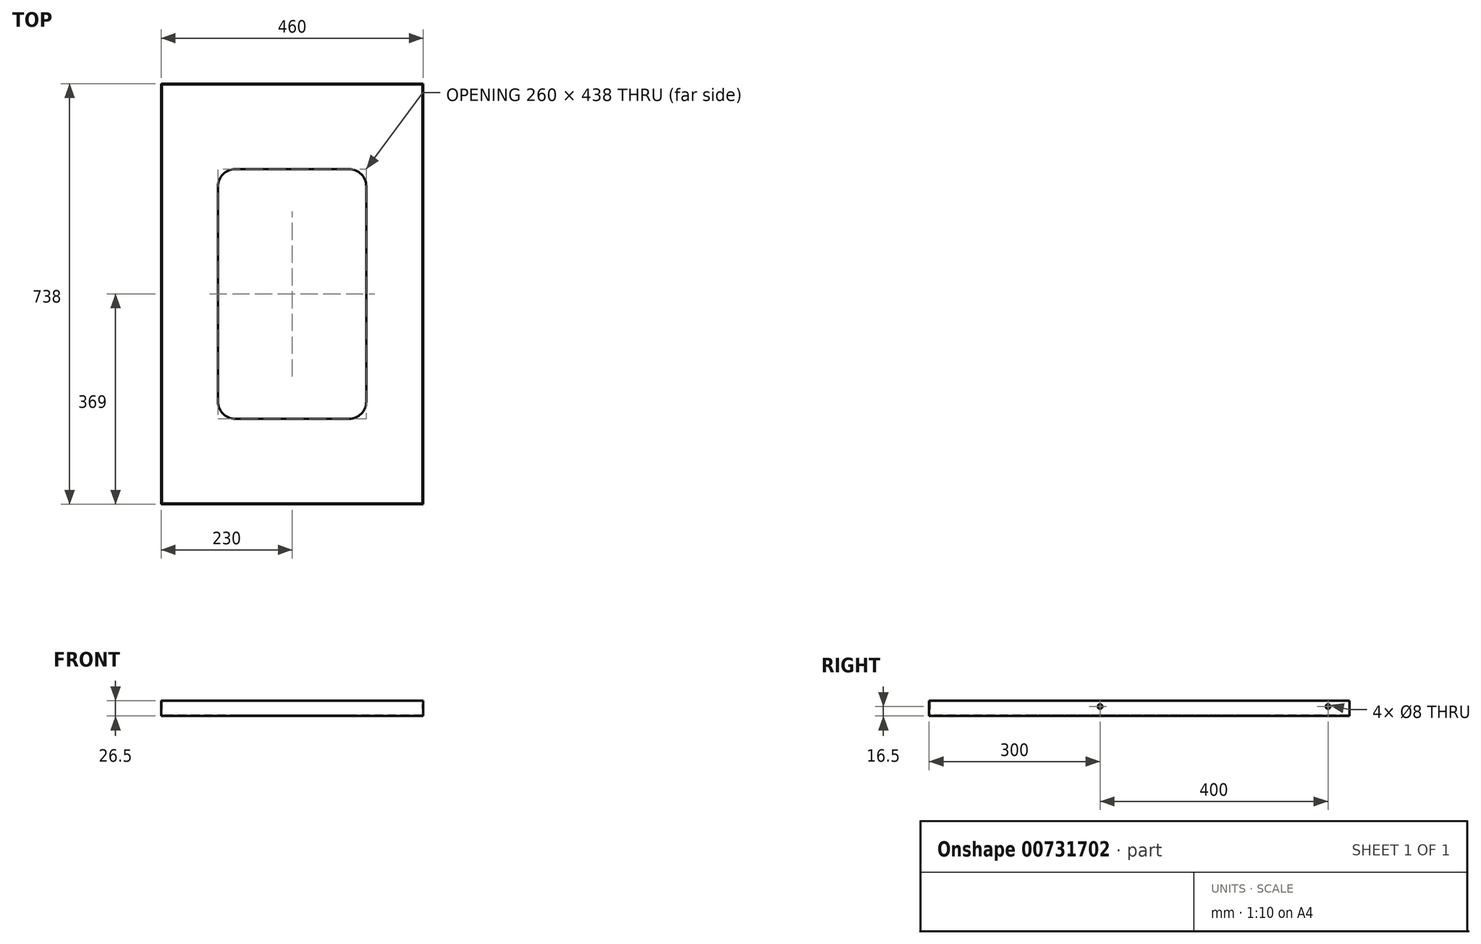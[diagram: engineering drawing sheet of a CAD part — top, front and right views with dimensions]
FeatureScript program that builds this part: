
annotation { "Feature Type Name" : "Feature", "Feature Type Description" : "" }
export const myFeature = defineFeature(function(context is Context, id is Id, definition is map)
    precondition{}
    {
        {
            var Q0;
            Q0=qCreatedBy(makeId("Top.planeOp"),FACE);
            var sketch = newSketch(context, id + "F0", { "sketchPlane" : qUnion([Q0])});
            skLineSegment(sketch, "E0.bottom", {"start": v(230, 369) * mm, "end": v(-230, 369) * mm});
            skLineSegment(sketch, "E0.top", {"start": v(230, -369) * mm, "end": v(-230, -369) * mm});
            skLineSegment(sketch, "E0.left", {"start": v(230, 369) * mm, "end": v(230, -369) * mm});
            skLineSegment(sketch, "E0.right", {"start": v(-230, 369) * mm, "end": v(-230, -369) * mm});
            skPoint(sketch, "E0.middle", {"position": v(0, 0) * mm});
            skLineSegment(sketch, "E1.bottom", {"start": v(100, 219) * mm, "end": v(-100, 219) * mm});
            skLineSegment(sketch, "E1.top", {"start": v(100, -219) * mm, "end": v(-100, -219) * mm});
            skLineSegment(sketch, "E1.left", {"start": v(130, 189) * mm, "end": v(130, -189) * mm});
            skLineSegment(sketch, "E1.right", {"start": v(-130, 189) * mm, "end": v(-130, -189) * mm});
            skPoint(sketch, "E2.visualSharp", {"position": v(-130, -219) * mm});
            skArc(sketch, "E2.filletArc", {"start": v(-130, -189) * mm, "mid": v(-121.21, -210.21) * mm, "end": v(-100, -219) * mm});
            skPoint(sketch, "E3.visualSharp", {"position": v(130, -219) * mm});
            skArc(sketch, "E3.filletArc", {"start": v(100, -219) * mm, "mid": v(121.21, -210.21) * mm, "end": v(130, -189) * mm});
            skPoint(sketch, "E4.visualSharp", {"position": v(130, 219) * mm});
            skArc(sketch, "E4.filletArc", {"start": v(130, 189) * mm, "mid": v(121.21, 210.21) * mm, "end": v(100, 219) * mm});
            skPoint(sketch, "E5.visualSharp", {"position": v(-130, 219) * mm});
            skArc(sketch, "E5.filletArc", {"start": v(-100, 219) * mm, "mid": v(-121.21, 210.21) * mm, "end": v(-130, 189) * mm});
            skSolve(sketch);
        }
        {
            var Q0;
            Q0=makeQuery(id+"F0.imprint","IMPRINT",FACE,{"disambiguationData":[TD([[makeQuery(id+"F0.imprint","IMPRINT",EDGE,{"derivedFrom":sQuery(id+"F0.wireOp",EDGE,"E0.bottom")}),1.0]])]});
            extrude(context, id + "F1", {"entities" : qUnion([Q0]), "depth" : 1.5 * mm, "offsetDistance" : 25 * mm});
        }
        {
            var Q0;
            Q0=makeQuery(id+"F1.opExtrude","CAP_FACE",FACE,{"disambiguationData":[OSD([sQuery(id+"F0.wireOp",EDGE,"E0.bottom"),sQuery(id+"F0.wireOp",EDGE,"E0.top"),sQuery(id+"F0.wireOp",EDGE,"E0.left"),sQuery(id+"F0.wireOp",EDGE,"E0.right"),sQuery(id+"F0.wireOp",EDGE,"E1.bottom"),sQuery(id+"F0.wireOp",EDGE,"E1.top"),sQuery(id+"F0.wireOp",EDGE,"E1.left"),sQuery(id+"F0.wireOp",EDGE,"E1.right"),sQuery(id+"F0.wireOp",EDGE,"E2.filletArc"),sQuery(id+"F0.wireOp",EDGE,"E3.filletArc"),sQuery(id+"F0.wireOp",EDGE,"E4.filletArc"),sQuery(id+"F0.wireOp",EDGE,"E5.filletArc")])],"isStart":false});
            var sketch = newSketch(context, id + "F2", { "sketchPlane" : qUnion([Q0])});
            skLineSegment(sketch, "E6.0", {"start": v(228.5, 367.5) * mm, "end": v(-228.5, 367.5) * mm});
            skLineSegment(sketch, "E6.1", {"start": v(228.5, 367.5) * mm, "end": v(228.5, -367.5) * mm});
            skLineSegment(sketch, "E6.2", {"start": v(228.5, -367.5) * mm, "end": v(-228.5, -367.5) * mm});
            skLineSegment(sketch, "E6.3", {"start": v(-228.5, 367.5) * mm, "end": v(-228.5, -367.5) * mm});
            skSolve(sketch);
        }
        {
            var Q0;
            Q0=makeQuery(id+"F2.imprint","IMPRINT",FACE,{"disambiguationData":[TD([[makeQuery(id+"F2.imprint","IMPRINT",EDGE,{"derivedFrom":sQuery(id+"F2.wireOp",EDGE,"E6.0")}),-1.0]])]});
            extrude(context, id + "F3", {"entities" : qUnion([Q0]), "operationType" : NewBodyOperationType.ADD, "depth" : 25 * mm, "offsetDistance" : 25 * mm});
        }
        {
            var Q0;
            {var subQ0=sQuery(id+"F0.wireOp",EDGE,"E0.left");Q0=makeQuery(id+"F3.boolean.opBoolean","MERGE",FACE,{"derivedFrom":[makeQuery(id+"F1.opExtrude","SWEPT_FACE",FACE,{"disambiguationData":[OSD([subQ0])]}),makeQuery(id+"F3.opExtrude","SWEPT_FACE",FACE,{"disambiguationData":[OSD([subQ0])]})]});}
            var sketch = newSketch(context, id + "F4", { "sketchPlane" : qUnion([Q0])});
            skCircle(sketch, "E7", {"center": v(331, 16.5) * mm, "radius": 4 * mm});
            skCircle(sketch, "E8", {"center": v(-69, 16.5) * mm, "radius": 4 * mm});
            skSolve(sketch);
        }
        {
            var Q0;
            Q0=makeQuery(id+"F4.imprint","IMPRINT",FACE,{"disambiguationData":[TD([[makeQuery(id+"F4.imprint","IMPRINT",EDGE,{"derivedFrom":sQuery(id+"F4.wireOp",EDGE,"E8")}),1.0]])]});
            var Q1;
            Q1=makeQuery(id+"F4.imprint","IMPRINT",FACE,{"disambiguationData":[TD([[makeQuery(id+"F4.imprint","IMPRINT",EDGE,{"derivedFrom":sQuery(id+"F4.wireOp",EDGE,"E7")}),1.0]])]});
            extrude(context, id + "F5", {"entities" : qUnion([Q0, Q1]), "operationType" : NewBodyOperationType.REMOVE, "oppositeDirection" : true, "depth" : 25 * mm, "offsetDistance" : 25 * mm});
        }
        {
            var Q0;
            {var subQ0=sQuery(id+"F0.wireOp",EDGE,"E0.right");Q0=makeQuery(id+"F3.boolean.opBoolean","MERGE",FACE,{"derivedFrom":[makeQuery(id+"F1.opExtrude","SWEPT_FACE",FACE,{"disambiguationData":[OSD([subQ0])]}),makeQuery(id+"F3.opExtrude","SWEPT_FACE",FACE,{"disambiguationData":[OSD([subQ0])]})]});}
            var sketch = newSketch(context, id + "F6", { "sketchPlane" : qUnion([Q0])});
            skCircle(sketch, "E9", {"center": v(-331, 16.5) * mm, "radius": 4 * mm});
            skCircle(sketch, "E10", {"center": v(69, 16.5) * mm, "radius": 4 * mm});
            skSolve(sketch);
        }
        {
            var Q0;
            Q0 = qSketchRegion(id + "F6", true);
            extrude(context, id + "F7", {"entities" : qUnion([Q0]), "operationType" : NewBodyOperationType.REMOVE, "oppositeDirection" : true, "depth" : 25 * mm, "offsetDistance" : 25 * mm});
        }
    });
